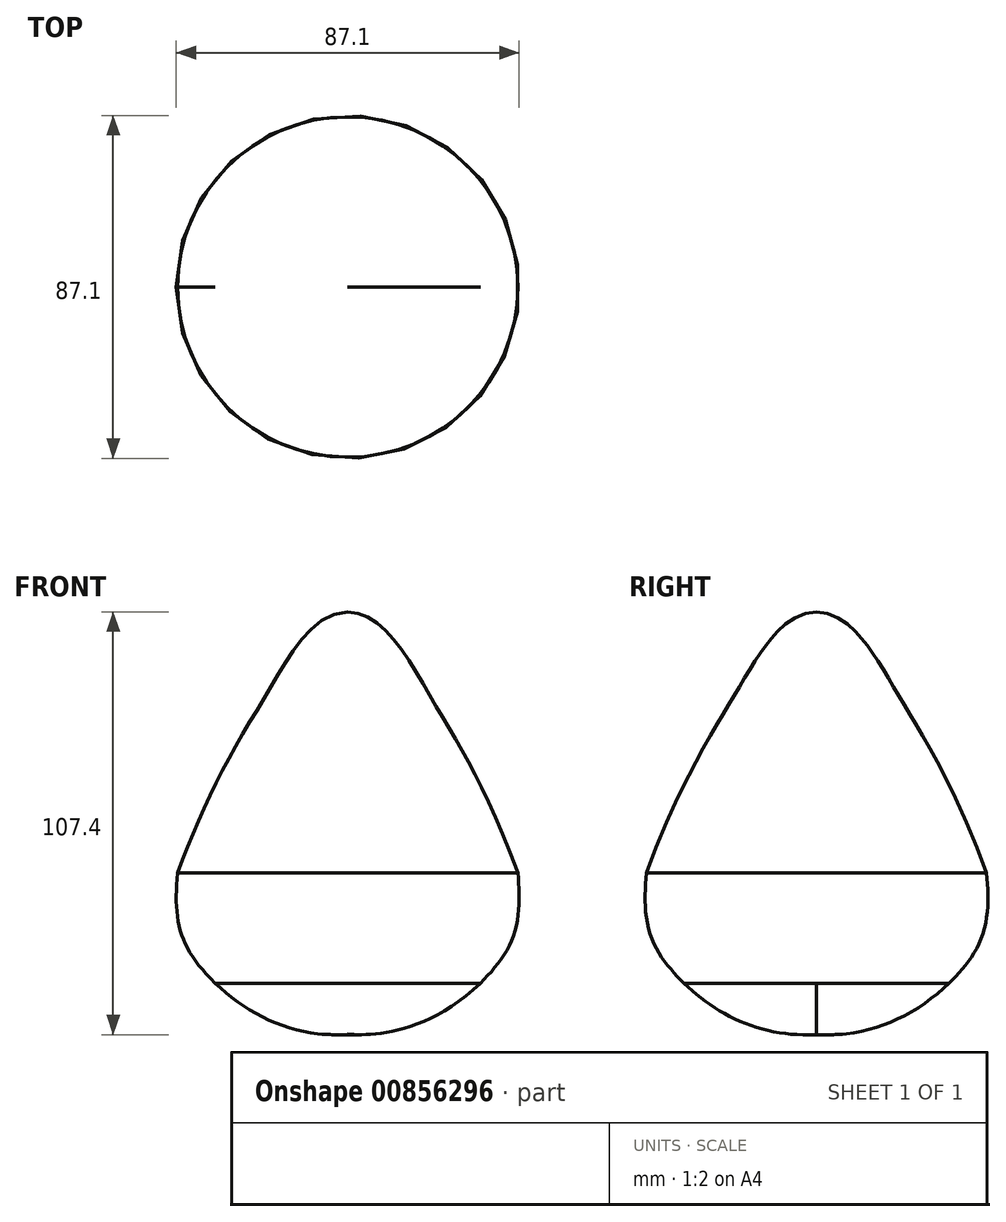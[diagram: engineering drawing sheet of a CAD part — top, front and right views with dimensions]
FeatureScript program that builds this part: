
annotation { "Feature Type Name" : "Feature", "Feature Type Description" : "" }
export const myFeature = defineFeature(function(context is Context, id is Id, definition is map)
    precondition{}
    {
        {
            var Q0;
            Q0=qCreatedBy(makeId("Front.planeOp"),FACE);
            var sketch = newSketch(context, id + "F0", { "sketchPlane" : qUnion([Q0])});
            skFitSpline(sketch, "E0", {"points": [v(26.9, 42.94) * mm, v(47.67, 21.89) * mm, v(70.13, -23.3) * mm], "startDerivative": vector(61.91, 0) * mm, "endDerivative": vector(46.22, -123.43) * mm});
            skFitSpline(sketch, "E1", {"points": [v(60.58, -51.37) * mm, v(26.9, -64.28) * mm], "startDerivative": vector(-42.1, -40.42) * mm, "endDerivative": vector(-16, 1.68) * mm});
            skLineSegment(sketch, "E2", {"start": v(26.9, 42.94) * mm, "end": v(26.9, -64.28) * mm});
            skLineSegment(sketch, "E3", {"start": v(26.9, 55.91) * mm, "end": v(26.9, -84.92) * mm, "construction": true});
            skFitSpline(sketch, "E4", {"points": [v(70.13, -23.3) * mm, v(60.58, -51.37) * mm], "startDerivative": vector(3.3, -36.92) * mm, "endDerivative": vector(-27.94, -27.3) * mm});
            skSolve(sketch);
        }
        {
            var Q0;
            Q0=sQuery(id+"F0.wireOp",EDGE,"E0");
            var Q1;
            Q1=sQuery(id+"F0.wireOp",EDGE,"E4");
            var Q2;
            Q2=sQuery(id+"F0.wireOp",EDGE,"E1");
            var Q3;
            Q3=sQuery(id+"F0.wireOp",EDGE,"E3");
            revolve(context, id + "F1", {"bodyType" : ToolBodyType.SURFACE, "surfaceOperationType" : NewSurfaceOperationType.NEW, "surfaceEntities" : qUnion([Q0, Q1, Q2]), "axis" : qUnion([Q3]), "revolveType" : RevolveType.FULL});
        }
    });
